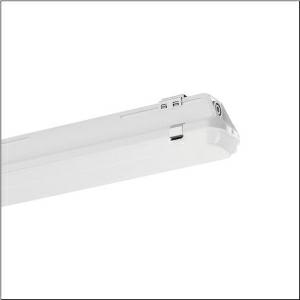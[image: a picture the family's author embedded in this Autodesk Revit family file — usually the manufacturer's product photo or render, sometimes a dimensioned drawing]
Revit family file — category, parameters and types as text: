
# Revit family: monsun_r__12_51fp22mp4b0q_ecbd
name_source: partatom
category: Lighting Fixtures
units: mm (PartAtom-declared; Revit-internal decimal feet)

## family parameters
Cut with Voids When Loaded = No
Host = Face
Light Source = No
Part Type = Normal
Room Calculation Point = No
Round Connector Dimension = Use Diameter
Shared = No

## types (1)
- --- (1 x LED, 10520 lm, 66.2 W, 4000K)
    Apparent Load = 66 VA
    CIE Flux Codes = 49 78 94 96 100
    Color Rendering = 80
    Color Temperature = 4000K
    Default Elevation = 1800 mm
    Description = Monsun® 12, damp-proof luminaire, chain hanger, primary light control with lens, primary optical cover: enclosure, of PC, light emission: direct distribution, primary light characteristic: symmetric, installation type: suspended mounting, surface-mounted, horizontal mounting, vertical mounting, LED rated luminous flux: 10.520 lm, light colour: 840, colour temperature: 4000K, control gear: ECG, with terminal, 3-pole, max. 2.5mm², mains connection: 220..240V, AC, 50/60Hz, rated input power: 66W, luminaire housing, of glass-fibre reinforced polyester, uncoated, bright grey, length: 1.590 mm, width: 90 mm, height: 88mm, clip for enclosure, of stainless steel (V2A), ceiling mounting element, of stainless steel (V2A), chain hanger, of stainless steel (V2A), protection rating (complete): IP66, insulation class (complete): insulation class I (protective earthing), certification: CE, ENEC, VDE, protection symbol: D, impact resistance: IK08, permissible ambient temperature for indoor applications: -35..+35°C, standard: EN 50419, EN 60598-2-1, no direct snow, no direct sun, no direct rain, for indoor or canopied outdoor use, corresponds to IFS (International Featured Standards) requirements for safety and quality in the food industry, packaging unit: 1 piece
    Height = 89 mm
    Lamp = 1 x LED
    Lamp Light Flux = 10520 lm
    Lamp Power = 66.2 W
    Lamp count = 1
    Length = 1590 mm
    Luminous efficacy = 159 lm/W
    Manufacturer = Siteco
    ModVariant = No
    Model = 51FP22MP4B0Q
    Mounting Place = Ceiling
    Mounting Type = Pendant
    Number of Poles = 1
    OnlyDefault = Yes
    Power Factor = 1
    Product Name = Monsun® 12
    Product group = damp-proof luminaire | ceiling pendant
    ProductGroupID = 908
    Protection Class = Protection class I
    Protection Degree = IP 66
    RLX_Detail_Level = 1
    RlxData = <blob elided: 89521 chars, md5=bbb3161f>
    Socket = socket
    Standby Power = 0 W
    System Light Flux = 10520 lm
    System Power = 66 W
    Type Comments = factory setting: luminous flux: 100 % | (A | C | E) | 155 mA
    Type Image = l_1004748.jpg
    URL = http://relux.com
    VarID = @adj_134031
    Voltage = 0 V
    Weight = 0.00 kg
    Width = 90 mm

## geometry (parser evidence)
native form markers: Blend x4, Sweep x12
no freeform markers — native parametric forms only
